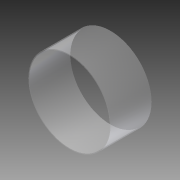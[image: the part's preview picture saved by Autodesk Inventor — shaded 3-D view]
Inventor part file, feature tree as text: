
AUTODESK INVENTOR PART (.ipt)
format: ipt  version: 2012 (Build 160160000, 160)  size: 79,872 bytes
history: native  units: in
note: dims shown in document units (in); Inventor stores cm internally (conversion verified against a paired STEP export)
features: extrude x1, sketch x1
ambient origin geometry x8: Origin, YZ Plane, XZ Plane, XY Plane, X Axis, Y Axis, Z Axis, Center Point
bodies: Solid1 (feature_tree)
feature tree (2):
  extrude  "Extrusion1"  Depth=11.75in
  sketch  "Sketch1"  dims[d0=12.0in d1=11.75in d2=6.0in d3=0.0in]
